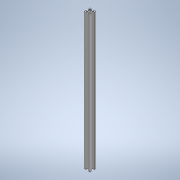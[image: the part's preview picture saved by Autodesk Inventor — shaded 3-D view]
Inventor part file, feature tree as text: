
AUTODESK INVENTOR PART (.ipt)
format: ipt  version: 2021 (Build 250183000, 183)  size: 356,864 bytes
history: native  units: mm
features: sketch x5, hole x3, other x2, extrude x2, fillet x2, pattern_circular x1, projected_geometry x1
ambient origin geometry x8: Origin, YZ Plane, XZ Plane, XY Plane, X Axis, Y Axis, Z Axis, Center Point
bodies: Body1 (feature_tree)
feature tree (16):
  other  "實體1"
  extrude  "擠出1"  Depth=20.0mm
  extrude  "擠出2"  Depth=20.0mm
  fillet  "圓角1"  Radius=462.0mm
  pattern_circular  "環形陣列1"  [2 undecoded]
  hole  "孔1"  [1 undecoded]
  fillet  "圓角2"  Radius=6.2mm
  hole  "孔2"  [1 undecoded]
  hole  "孔3"  [1 undecoded]
  sketch  "草圖1"
  sketch  "草圖2"
  projected_geometry  "投影迴路1"
  sketch  "草圖3"
  sketch  "草圖4"
  sketch  "草圖5"
  other  "投影切割邊1"
note: 5 required parameter values undecoded (feature->parameter linkage not recoverable at this tier; creation-order binding heuristic only, values carry confidence <= 0.55)
